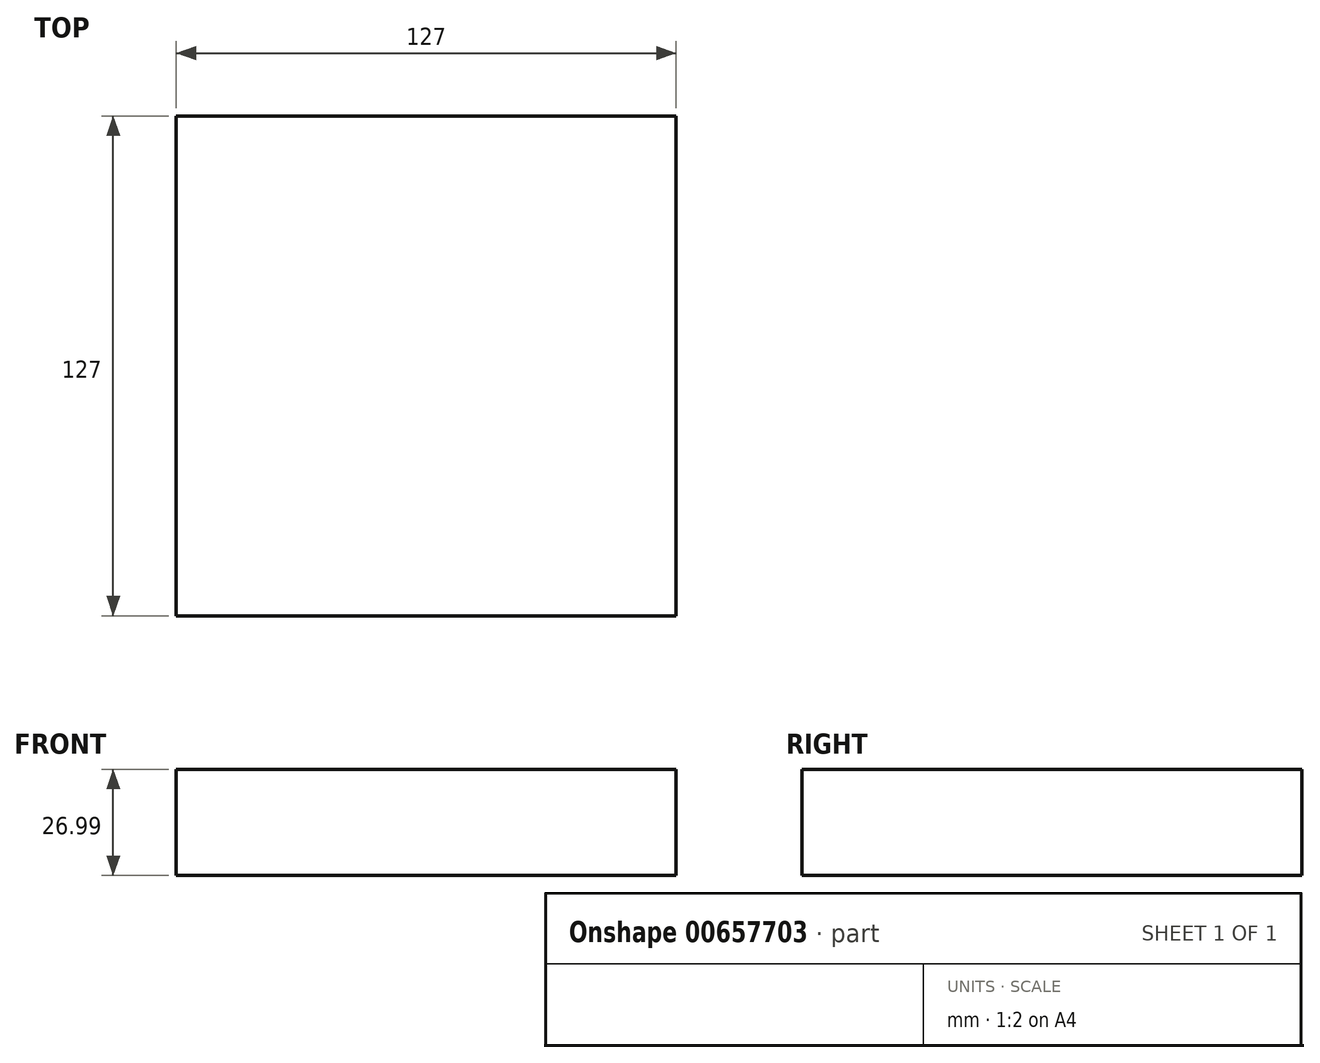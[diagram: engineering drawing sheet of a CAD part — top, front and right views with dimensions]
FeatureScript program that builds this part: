
annotation { "Feature Type Name" : "Feature", "Feature Type Description" : "" }
export const myFeature = defineFeature(function(context is Context, id is Id, definition is map)
    precondition{}
    {
        {
            var Q0;
            Q0=qCreatedBy(makeId("Top.planeOp"),FACE);
            var sketch = newSketch(context, id + "F0", { "sketchPlane" : qUnion([Q0])});
            skLineSegment(sketch, "E0.bottom", {"start": v(0, 0) * mm, "end": v(127, 0) * mm});
            skLineSegment(sketch, "E0.top", {"start": v(0, -127) * mm, "end": v(127, -127) * mm});
            skLineSegment(sketch, "E0.left", {"start": v(0, 0) * mm, "end": v(0, -127) * mm});
            skLineSegment(sketch, "E0.right", {"start": v(127, 0) * mm, "end": v(127, -127) * mm});
            skSolve(sketch);
        }
        {
            var Q0;
            Q0=makeQuery(id+"F0.imprint","IMPRINT",FACE,{"disambiguationData":[TD([[makeQuery(id+"F0.imprint","IMPRINT",EDGE,{"derivedFrom":sQuery(id+"F0.wireOp",EDGE,"E0.bottom")}),-1.0]])]});
            extrude(context, id + "F1", {"entities" : qUnion([Q0]), "depth" : 26.99 * mm, "offsetDistance" : 25.4 * mm});
        }
    });
